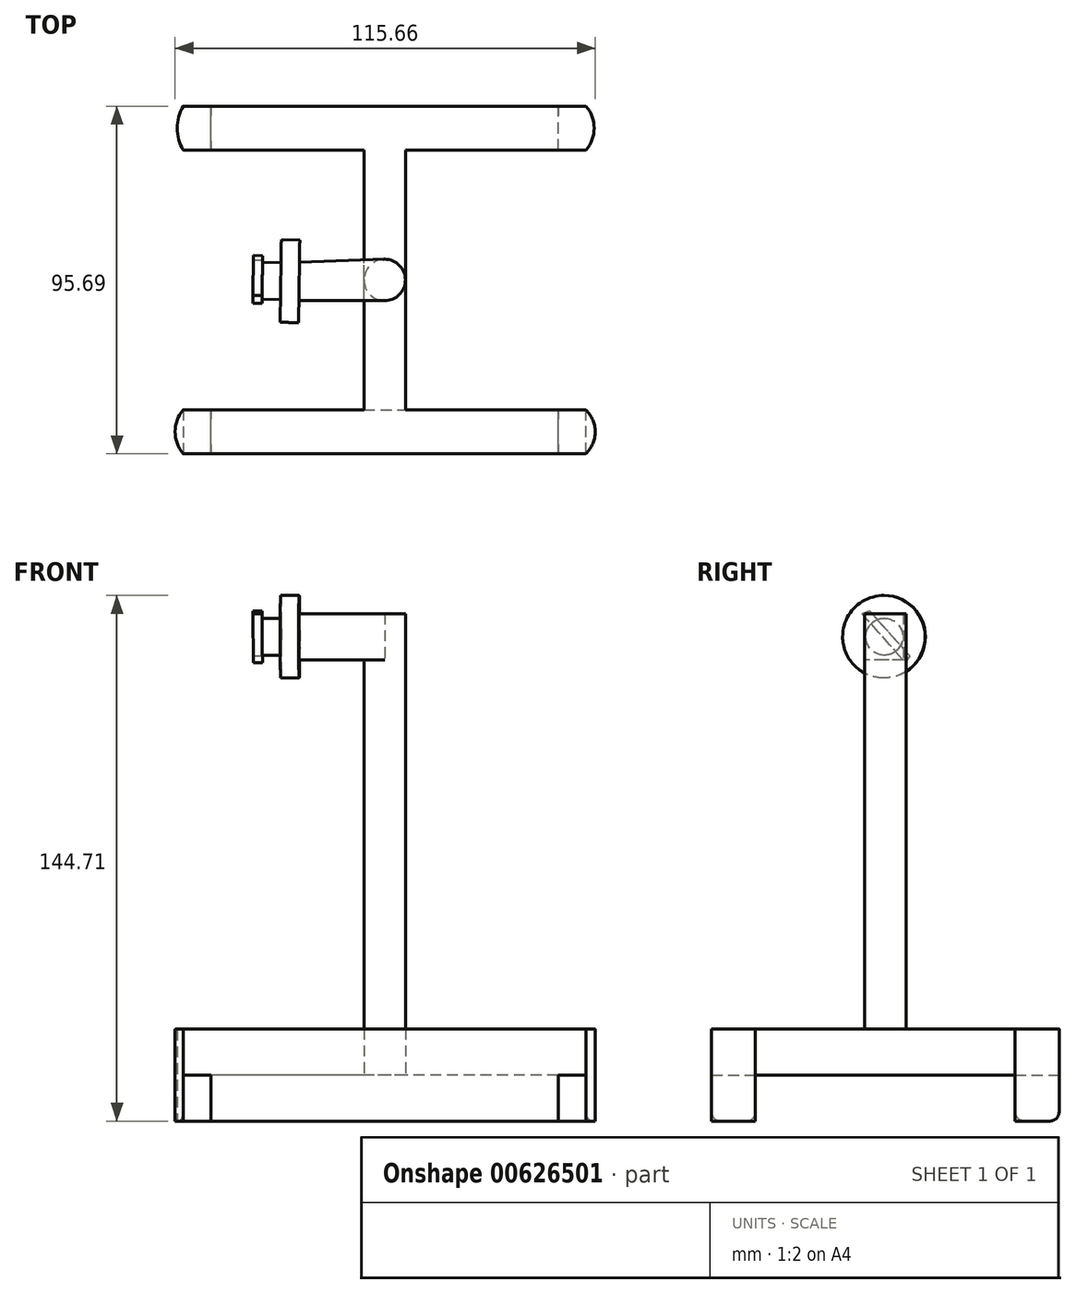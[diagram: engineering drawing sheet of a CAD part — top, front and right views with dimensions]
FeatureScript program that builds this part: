
annotation { "Feature Type Name" : "Feature", "Feature Type Description" : "" }
export const myFeature = defineFeature(function(context is Context, id is Id, definition is map)
    precondition{}
    {
        {
            var Q0;
            Q0=qCreatedBy(makeId("Top.planeOp"),FACE);
            var sketch = newSketch(context, id + "F0", { "sketchPlane" : qUnion([Q0])});
            skLineSegment(sketch, "E0.bottom", {"start": v(49.68, 42.92) * mm, "end": v(-61.22, 42.92) * mm});
            skLineSegment(sketch, "E0.top", {"start": v(49.68, -52.77) * mm, "end": v(-61.22, -52.77) * mm});
            skLineSegment(sketch, "E0.left", {"start": v(49.68, 42.92) * mm, "end": v(49.68, 30.82) * mm});
            skLineSegment(sketch, "E0.right", {"start": v(-61.22, 42.92) * mm, "end": v(-61.22, 30.82) * mm});
            skLineSegment(sketch, "E1", {"start": v(49.68, 30.82) * mm, "end": v(0, 30.82) * mm});
            skLineSegment(sketch, "E2", {"start": v(-61.22, -40.67) * mm, "end": v(-11.4, -40.67) * mm});
            skLineSegment(sketch, "E3", {"start": v(0, 30.82) * mm, "end": v(0, -40.67) * mm});
            skLineSegment(sketch, "E4", {"start": v(-11.4, -40.67) * mm, "end": v(-11.4, 30.82) * mm});
            skLineSegment(sketch, "E5.trimOffspring", {"start": v(-61.22, -40.67) * mm, "end": v(-61.22, -52.77) * mm});
            skLineSegment(sketch, "E6.trimOffspring", {"start": v(49.68, -40.67) * mm, "end": v(49.68, -52.77) * mm});
            skLineSegment(sketch, "E7.trimOffspring", {"start": v(0, -40.67) * mm, "end": v(49.68, -40.67) * mm});
            skLineSegment(sketch, "E8.trimOffspring", {"start": v(-11.4, 30.82) * mm, "end": v(-61.22, 30.82) * mm});
            skArc(sketch, "E9", {"start": v(49.68, 30.82) * mm, "mid": v(51.96, 36.87) * mm, "end": v(49.68, 42.92) * mm});
            skArc(sketch, "E10", {"start": v(49.68, -52.77) * mm, "mid": v(52.26, -46.72) * mm, "end": v(49.68, -40.67) * mm});
            skArc(sketch, "E11", {"start": v(-61.22, 42.92) * mm, "mid": v(-62.84, 36.87) * mm, "end": v(-61.22, 30.82) * mm});
            skArc(sketch, "E12", {"start": v(-61.22, -40.67) * mm, "mid": v(-63.4, -46.72) * mm, "end": v(-61.22, -52.77) * mm});
            skSolve(sketch);
        }
        {
            var Q0;
            Q0 = qSketchRegion(id + "F0", true);
            extrude(context, id + "F1", {"entities" : qUnion([Q0]), "depth" : 25.4 * mm, "offsetDistance" : 25.4 * mm});
        }
        {
            var Q0;
            Q0=makeQuery(id+"F1.opExtrude","CAP_FACE",FACE,{"disambiguationData":[OSD([sQuery(id+"F0.wireOp",EDGE,"E0.bottom"),sQuery(id+"F0.wireOp",EDGE,"E0.top"),sQuery(id+"F0.wireOp",EDGE,"E1"),sQuery(id+"F0.wireOp",EDGE,"E2"),sQuery(id+"F0.wireOp",EDGE,"E3"),sQuery(id+"F0.wireOp",EDGE,"E4"),sQuery(id+"F0.wireOp",EDGE,"E7.trimOffspring"),sQuery(id+"F0.wireOp",EDGE,"E8.trimOffspring"),sQuery(id+"F0.wireOp",EDGE,"E9"),sQuery(id+"F0.wireOp",EDGE,"E10"),sQuery(id+"F0.wireOp",EDGE,"E11"),sQuery(id+"F0.wireOp",EDGE,"E12")])],"isStart":true});
            var sketch = newSketch(context, id + "F2", { "sketchPlane" : qUnion([Q0])});
            skLineSegment(sketch, "E13", {"start": v(-61.22, 52.77) * mm, "end": v(49.68, 52.77) * mm});
            skLineSegment(sketch, "E14", {"start": v(49.68, 52.77) * mm, "end": v(49.68, 40.67) * mm});
            skLineSegment(sketch, "E15", {"start": v(49.68, 40.67) * mm, "end": v(-61.22, 40.67) * mm});
            skLineSegment(sketch, "E16", {"start": v(-61.22, 40.67) * mm, "end": v(-61.22, 52.77) * mm});
            skLineSegment(sketch, "E17", {"start": v(-61.22, -30.82) * mm, "end": v(49.68, -30.82) * mm});
            skLineSegment(sketch, "E18", {"start": v(49.68, -30.82) * mm, "end": v(49.68, -42.92) * mm});
            skLineSegment(sketch, "E19", {"start": v(49.68, -42.92) * mm, "end": v(-61.22, -42.92) * mm});
            skLineSegment(sketch, "E20", {"start": v(-61.22, -42.92) * mm, "end": v(-61.22, -30.82) * mm});
            skLineSegment(sketch, "E21", {"start": v(-61.22, -30.82) * mm, "end": v(-53.6, -30.82) * mm});
            skLineSegment(sketch, "E22", {"start": v(49.68, -30.82) * mm, "end": v(42.06, -30.82) * mm});
            skLineSegment(sketch, "E23", {"start": v(49.68, 52.77) * mm, "end": v(42.06, 52.77) * mm});
            skLineSegment(sketch, "E24", {"start": v(-61.22, 52.77) * mm, "end": v(-53.6, 52.77) * mm});
            skLineSegment(sketch, "E25", {"start": v(-53.6, 52.77) * mm, "end": v(-53.6, 40.67) * mm});
            skLineSegment(sketch, "E26", {"start": v(42.06, 52.77) * mm, "end": v(42.06, 40.67) * mm});
            skLineSegment(sketch, "E27", {"start": v(42.06, -30.82) * mm, "end": v(42.06, -42.92) * mm});
            skLineSegment(sketch, "E28", {"start": v(-53.6, -30.82) * mm, "end": v(-53.6, -42.92) * mm});
            skSolve(sketch);
        }
        {
            var Q0;
            Q0=makeQuery(id+"F2.imprint","IMPRINT",FACE,{"disambiguationData":[TD([[makeQuery(id+"F2.imprint","IMPRINT",EDGE,{"derivedFrom":sQuery(id+"F2.wireOp",EDGE,"E13")}),1.0]])]});
            var Q1;
            {var subQ4=sQuery(id+"F2.wireOp",EDGE,"E27");Q1=makeQuery(id+"F2.imprint","IMPRINT",FACE,{"disambiguationData":[TD([[makeQuery(id+"F2.imprint","IMPRINT",EDGE,{"derivedFrom":subQ4}),-1.0]])]});}
            var Q2;
            {var subQ2=makeQuery(id+"F1.opExtrude","CAP_EDGE",EDGE,{"disambiguationData":[OSD([sQuery(id+"F0.wireOp",EDGE,"E3")])],"isStart":true});Q2=makeQuery(id+"F2.imprint","IMPRINT",FACE,{"disambiguationData":[TD([[makeQuery(id+"F2.imprint","IMPRINT",EDGE,{"derivedFrom":subQ2}),1.0]])]});}
            extrude(context, id + "F3", {"entities" : qUnion([Q0, Q1, Q2]), "operationType" : NewBodyOperationType.REMOVE, "oppositeDirection" : true, "depth" : 12.7 * mm, "offsetDistance" : 25.4 * mm});
        }
        {
            var Q0;
            Q0=makeQuery(id+"F1.opExtrude","CAP_EDGE",EDGE,{"disambiguationData":[OSD([sQuery(id+"F0.wireOp",EDGE,"E12")])],"isStart":false});
            var Q1;
            Q1=makeQuery(id+"F1.opExtrude","CAP_EDGE",EDGE,{"disambiguationData":[OSD([sQuery(id+"F0.wireOp",EDGE,"E10")])],"isStart":false});
            var Q2;
            Q2=makeQuery(id+"F1.opExtrude","CAP_EDGE",EDGE,{"disambiguationData":[OSD([sQuery(id+"F0.wireOp",EDGE,"E9")])],"isStart":false});
            var Q3;
            Q3=makeQuery(id+"F1.opExtrude","CAP_EDGE",EDGE,{"disambiguationData":[OSD([sQuery(id+"F0.wireOp",EDGE,"E11")])],"isStart":false});
            fillet(context, id + "F4", {"entities" : qUnion([Q0, Q1, Q2, Q3]), "radius" : 0.25 * mm, "tangentPropagation" : true, "allowEdgeOverflow" : false});
        }
        {
            var Q0;
            Q0=makeQuery(id+"F1.opExtrude","CAP_EDGE",EDGE,{"disambiguationData":[OSD([sQuery(id+"F0.wireOp",EDGE,"E8.trimOffspring")])],"isStart":true});
            var Q1;
            {var subQ0=sQuery(id+"F0.wireOp",EDGE,"E12");var subQ1=sQuery(id+"F0.wireOp",EDGE,"E0.top");Q1=makeQuery(id+"F3.boolean.opBoolean","SPLIT",EDGE,{"disambiguationData":[TD([makeQuery(id+"F1.opExtrude","SWEPT_FACE",FACE,{"disambiguationData":[OSD([subQ0])]})])],"derivedFrom":makeQuery(id+"F1.opExtrude","CAP_EDGE",EDGE,{"disambiguationData":[OSD([subQ1])],"isStart":true})});}
            var Q2;
            {var subQ0=sQuery(id+"F0.wireOp",EDGE,"E10");var subQ1=sQuery(id+"F0.wireOp",EDGE,"E0.top");Q2=makeQuery(id+"F3.boolean.opBoolean","SPLIT",EDGE,{"disambiguationData":[TD([makeQuery(id+"F1.opExtrude","SWEPT_FACE",FACE,{"disambiguationData":[OSD([subQ0])]})])],"derivedFrom":makeQuery(id+"F1.opExtrude","CAP_EDGE",EDGE,{"disambiguationData":[OSD([subQ1])],"isStart":true})});}
            var Q3;
            {var subQ0=sQuery(id+"F0.wireOp",EDGE,"E0.bottom");var subQ1=sQuery(id+"F0.wireOp",EDGE,"E9");Q3=makeQuery(id+"F3.boolean.opBoolean","SPLIT",EDGE,{"disambiguationData":[TD([makeQuery(id+"F1.opExtrude","SWEPT_FACE",FACE,{"disambiguationData":[OSD([subQ1])]})])],"derivedFrom":makeQuery(id+"F1.opExtrude","CAP_EDGE",EDGE,{"disambiguationData":[OSD([subQ0])],"isStart":true})});}
            var Q4;
            {var subQ0=sQuery(id+"F0.wireOp",EDGE,"E0.bottom");var subQ1=sQuery(id+"F0.wireOp",EDGE,"E11");Q4=makeQuery(id+"F3.boolean.opBoolean","SPLIT",EDGE,{"disambiguationData":[TD([makeQuery(id+"F1.opExtrude","SWEPT_FACE",FACE,{"disambiguationData":[OSD([subQ1])]})])],"derivedFrom":makeQuery(id+"F1.opExtrude","CAP_EDGE",EDGE,{"disambiguationData":[OSD([subQ0])],"isStart":true})});}
            var Q5;
            Q5=makeQuery(id+"F1.opExtrude","CAP_EDGE",EDGE,{"disambiguationData":[OSD([sQuery(id+"F0.wireOp",EDGE,"E2")])],"isStart":true});
            var Q6;
            Q6=makeQuery(id+"F1.opExtrude","CAP_EDGE",EDGE,{"disambiguationData":[OSD([sQuery(id+"F0.wireOp",EDGE,"E7.trimOffspring")])],"isStart":true});
            fillet(context, id + "F5", {"entities" : qUnion([Q0, Q1, Q2, Q3, Q4, Q5, Q6]), "radius" : 2.54 * mm, "tangentPropagation" : true, "allowEdgeOverflow" : false});
        }
        {
            var Q0;
            Q0=makeQuery(id+"F1.opExtrude","CAP_FACE",FACE,{"disambiguationData":[OSD([sQuery(id+"F0.wireOp",EDGE,"E0.bottom"),sQuery(id+"F0.wireOp",EDGE,"E0.top"),sQuery(id+"F0.wireOp",EDGE,"E1"),sQuery(id+"F0.wireOp",EDGE,"E2"),sQuery(id+"F0.wireOp",EDGE,"E3"),sQuery(id+"F0.wireOp",EDGE,"E4"),sQuery(id+"F0.wireOp",EDGE,"E7.trimOffspring"),sQuery(id+"F0.wireOp",EDGE,"E8.trimOffspring"),sQuery(id+"F0.wireOp",EDGE,"E9"),sQuery(id+"F0.wireOp",EDGE,"E10"),sQuery(id+"F0.wireOp",EDGE,"E11"),sQuery(id+"F0.wireOp",EDGE,"E12")])],"isStart":false});
            var sketch = newSketch(context, id + "F6", { "sketchPlane" : qUnion([Q0])});
            skCircle(sketch, "E29", {"center": v(-5.7, -4.93) * mm, "radius": 5.7 * mm});
            skLineSegment(sketch, "E30", {"start": v(0, -4.93) * mm, "end": v(0, 4.34) * mm});
            skLineSegment(sketch, "E31", {"start": v(0, 4.34) * mm, "end": v(-11.4, 4.34) * mm});
            skLineSegment(sketch, "E32", {"start": v(-11.4, 4.34) * mm, "end": v(-11.4, -14.9) * mm});
            skLineSegment(sketch, "E33", {"start": v(-11.4, -14.9) * mm, "end": v(0, -14.9) * mm});
            skLineSegment(sketch, "E34", {"start": v(0, -14.9) * mm, "end": v(0, 4.34) * mm});
            skPoint(sketch, "E35.end.orphan", {"position": v(-11.4, -4.93) * mm});
            skSolve(sketch);
        }
        {
            var Q0;
            {var subQ0=sQuery(id+"F6.wireOp",EDGE,"E29");var subQ1=makeQuery(id+"F6.imprint","INTERSECT",VERTEX,{"derivedFrom":[subQ0,sQuery(id+"F6.wireOp",EDGE,"E32")]});Q0=makeQuery(id+"F6.imprint","IMPRINT",FACE,{"disambiguationData":[TD([[makeQuery(id+"F6.imprint","IMPRINT",EDGE,{"disambiguationData":[TD([[subQ1,1.0]])],"derivedFrom":subQ0}),1.0]])]});}
            extrude(context, id + "F7", {"entities" : qUnion([Q0]), "operationType" : NewBodyOperationType.ADD, "depth" : 101.6 * mm, "offsetDistance" : 25.4 * mm});
        }
        {
            var Q0;
            Q0=makeQuery(id+"F7.opExtrude","CAP_FACE",FACE,{"disambiguationData":[OSD([sQuery(id+"F6.wireOp",EDGE,"E29")])],"isStart":false});
            var sketch = newSketch(context, id + "F8", { "sketchPlane" : qUnion([Q0])});
            skLineSegment(sketch, "E36", {"start": v(-5.7, -4.93) * mm, "end": v(-5.7, -10.62) * mm});
            skLineSegment(sketch, "E37", {"start": v(-5.7, -4.93) * mm, "end": v(-5.7, 0.77) * mm});
            skLineSegment(sketch, "E38", {"start": v(-5.7, 0.77) * mm, "end": v(-29.18, 0) * mm});
            skLineSegment(sketch, "E39", {"start": v(-5.7, -10.62) * mm, "end": v(-29.33, -10.62) * mm});
            skLineSegment(sketch, "E40", {"start": v(-29.18, 0) * mm, "end": v(-29.33, -10.62) * mm});
            skPoint(sketch, "E41.end.orphan", {"position": v(-29.18, -4.93) * mm});
            skSolve(sketch);
        }
        {
            var Q0;
            Q0 = qSketchRegion(id + "F8", true);
            var Q1;
            {var subQ0=sQuery(id+"F8.wireOp",EDGE,"E36");Q1=makeQuery(id+"F8.imprint","IMPRINT",FACE,{"disambiguationData":[TD([[makeQuery(id+"F8.imprint","IMPRINT",EDGE,{"derivedFrom":subQ0}),1.0]])]});}
            extrude(context, id + "F9", {"entities" : qUnion([Q0, Q1]), "operationType" : NewBodyOperationType.ADD, "depth" : 12.7 * mm, "offsetDistance" : 25.4 * mm});
        }
        {
            var Q0;
            Q0=makeQuery(id+"F9.opExtrude","SWEPT_FACE",FACE,{"disambiguationData":[OSD([sQuery(id+"F8.wireOp",EDGE,"E40")])]});
            var sketch = newSketch(context, id + "F10", { "sketchPlane" : qUnion([Q0])});
            skLineSegment(sketch, "E42", {"start": v(5.73, 139.7) * mm, "end": v(5.73, 127) * mm});
            skCircle(sketch, "E43", {"center": v(5.73, 133.35) * mm, "radius": 11.36 * mm});
            skSolve(sketch);
        }
        {
            var Q0;
            Q0 = qSketchRegion(id + "F10", true);
            extrude(context, id + "F11", {"entities" : qUnion([Q0]), "operationType" : NewBodyOperationType.ADD, "depth" : 5.08 * mm, "offsetDistance" : 25.4 * mm});
        }
        {
            var Q0;
            Q0=makeQuery(id+"F11.opExtrude","CAP_FACE",FACE,{"disambiguationData":[OSD([sQuery(id+"F10.wireOp",EDGE,"E43")])],"isStart":false});
            var sketch = newSketch(context, id + "F12", { "sketchPlane" : qUnion([Q0])});
            skCircle(sketch, "E44", {"center": v(5.73, 133.35) * mm, "radius": 5.1 * mm});
            skSolve(sketch);
        }
        {
            var Q0;
            Q0=makeQuery(id+"F12.imprint","IMPRINT",FACE,{"disambiguationData":[TD([[makeQuery(id+"F12.imprint","IMPRINT",EDGE,{"derivedFrom":sQuery(id+"F12.wireOp",EDGE,"E44")}),1.0]])]});
            extrude(context, id + "F13", {"entities" : qUnion([Q0]), "operationType" : NewBodyOperationType.ADD, "depth" : 5.08 * mm, "offsetDistance" : 25.4 * mm});
        }
        {
            var Q0;
            Q0=makeQuery(id+"F13.opExtrude","CAP_FACE",FACE,{"disambiguationData":[OSD([sQuery(id+"F12.wireOp",EDGE,"E44")])],"isStart":false});
            var sketch = newSketch(context, id + "F14", { "sketchPlane" : qUnion([Q0])});
            skLineSegment(sketch, "E45", {"start": v(11.98, 139.7) * mm, "end": v(0, 126.22) * mm});
            skPoint(sketch, "E46.start.orphan", {"position": v(5.73, 133.35) * mm});
            skLineSegment(sketch, "E47", {"start": v(9.82, 140.46) * mm, "end": v(-1.2, 128.06) * mm});
            skPoint(sketch, "E48.orphan", {"position": v(12.66, 126.24) * mm});
            skPoint(sketch, "E49.orphan", {"position": v(-1.2, 140.46) * mm});
            skLineSegment(sketch, "E50", {"start": v(-1.2, 128.06) * mm, "end": v(0.02, 126.24) * mm});
            skPoint(sketch, "E51.top.end.orphan", {"position": v(-1.2, 126.24) * mm});
            skLineSegment(sketch, "E52", {"start": v(9.82, 140.46) * mm, "end": v(11.98, 139.7) * mm});
            skPoint(sketch, "E53.orphan", {"position": v(12.66, 140.46) * mm});
            skSolve(sketch);
        }
        {
            var Q0;
            {var subQ0=sQuery(id+"F14.wireOp",EDGE,"E45");var subQ1=makeQuery(id+"F13.opExtrude","CAP_EDGE",EDGE,{"disambiguationData":[OSD([sQuery(id+"F12.wireOp",EDGE,"E44")])],"isStart":false});var subQ2=makeQuery(id+"F14.imprint","INTERSECT",VERTEX,{"disambiguationData":[OD(0.0)],"derivedFrom":[subQ1,subQ0]});Q0=makeQuery(id+"F14.imprint","IMPRINT",FACE,{"disambiguationData":[TD([[makeQuery(id+"F14.imprint","IMPRINT",EDGE,{"disambiguationData":[TD([[subQ2,-1.0]])],"derivedFrom":subQ0}),-1.0]])]});}
            var Q1;
            {var subQ0=sQuery(id+"F14.wireOp",EDGE,"E50");Q1=makeQuery(id+"F14.imprint","IMPRINT",FACE,{"disambiguationData":[TD([[makeQuery(id+"F14.imprint","IMPRINT",EDGE,{"derivedFrom":subQ0}),1.0]])]});}
            var Q2;
            {var subQ0=sQuery(id+"F14.wireOp",EDGE,"E52");Q2=makeQuery(id+"F14.imprint","IMPRINT",FACE,{"disambiguationData":[TD([[makeQuery(id+"F14.imprint","IMPRINT",EDGE,{"derivedFrom":subQ0}),-1.0]])]});}
            extrude(context, id + "F15", {"entities" : qUnion([Q0, Q1, Q2]), "operationType" : NewBodyOperationType.ADD, "depth" : 2.54 * mm, "offsetDistance" : 25.4 * mm});
        }
    });
